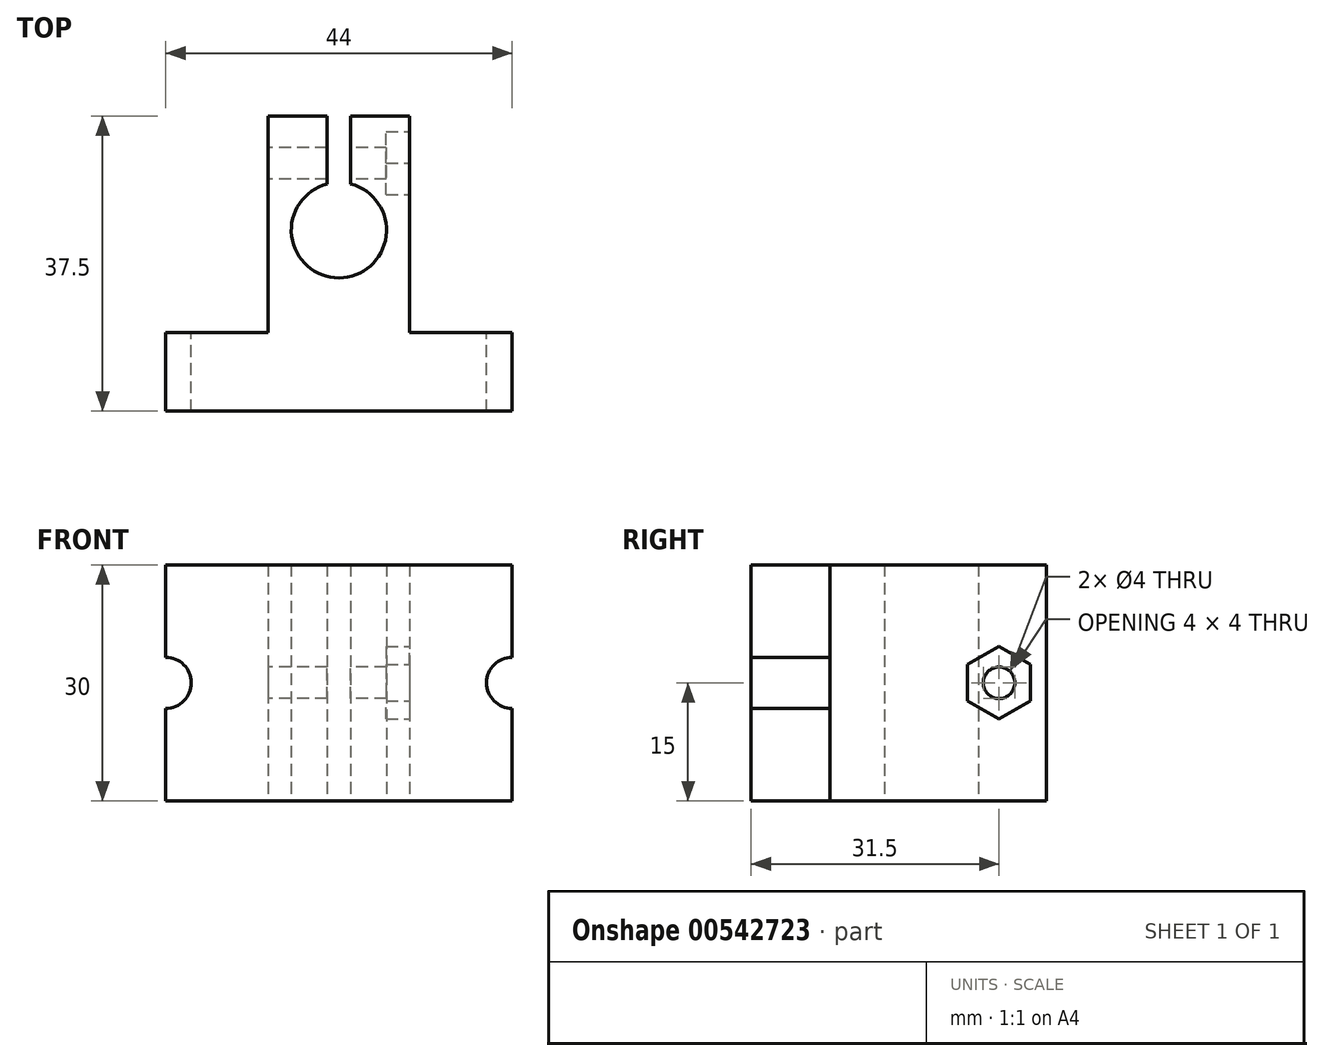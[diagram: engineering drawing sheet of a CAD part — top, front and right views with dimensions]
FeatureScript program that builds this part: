
annotation { "Feature Type Name" : "Feature", "Feature Type Description" : "" }
export const myFeature = defineFeature(function(context is Context, id is Id, definition is map)
    precondition{}
    {
        {
            var Q0;
            Q0=qCreatedBy(makeId("Top.planeOp"),FACE);
            var sketch = newSketch(context, id + "F0", { "sketchPlane" : qUnion([Q0])});
            skLineSegment(sketch, "E0", {"start": v(0, 0) * mm, "end": v(22, 0) * mm});
            skLineSegment(sketch, "E1", {"start": v(22, 0) * mm, "end": v(22, 10) * mm});
            skLineSegment(sketch, "E2", {"start": v(22, 10) * mm, "end": v(9, 10) * mm});
            skLineSegment(sketch, "E3", {"start": v(9, 10) * mm, "end": v(9, 37.5) * mm});
            skArc(sketch, "E4", {"start": v(-1.5, 28.86) * mm, "mid": v(0, 16.95) * mm, "end": v(1.5, 28.86) * mm});
            skLineSegment(sketch, "E5", {"start": v(9, 37.5) * mm, "end": v(1.5, 37.5) * mm});
            skLineSegment(sketch, "E6", {"start": v(1.5, 37.5) * mm, "end": v(1.5, 28.86) * mm});
            skLineSegment(sketch, "E7", {"start": v(0, 37.5) * mm, "end": v(0, 0) * mm, "construction": true});
            skLineSegment(sketch, "E8.MirrorCS", {"start": v(0, 0) * mm, "end": v(-22, 0) * mm});
            skLineSegment(sketch, "E9.MirrorCS", {"start": v(-22, 0) * mm, "end": v(-22, 10) * mm});
            skLineSegment(sketch, "E10.MirrorCS", {"start": v(-22, 10) * mm, "end": v(-9, 10) * mm});
            skLineSegment(sketch, "E11.MirrorCS", {"start": v(-9, 10) * mm, "end": v(-9, 37.5) * mm});
            skLineSegment(sketch, "E12.MirrorCS", {"start": v(-9, 37.5) * mm, "end": v(-1.5, 37.5) * mm});
            skLineSegment(sketch, "E13.MirrorCS", {"start": v(-1.5, 37.5) * mm, "end": v(-1.5, 28.86) * mm});
            skSolve(sketch);
        }
        {
            var Q0;
            Q0=makeQuery(id+"F0.imprint","IMPRINT",FACE,{"disambiguationData":[TD([[makeQuery(id+"F0.imprint","IMPRINT",EDGE,{"derivedFrom":sQuery(id+"F0.wireOp",EDGE,"E0")}),1.0]])]});
            extrude(context, id + "F1", {"entities" : qUnion([Q0]), "depth" : 30 * mm, "offsetDistance" : 25 * mm});
        }
        {
            var Q0;
            Q0=makeQuery(id+"F1.opExtrude","SWEPT_FACE",FACE,{"disambiguationData":[OSD([sQuery(id+"F0.wireOp",EDGE,"E10.MirrorCS")])]});
            var sketch = newSketch(context, id + "F2", { "sketchPlane" : qUnion([Q0])});
            skLineSegment(sketch, "E14", {"start": v(16, 15) * mm, "end": v(22, 15) * mm, "construction": true});
            skLineSegment(sketch, "E15.MirrorCS", {"start": v(-16, 15) * mm, "end": v(-22, 15) * mm, "construction": true});
            skSolve(sketch);
        }
        {
            var Q0;
            Q0=sQuery(id+"F2.wireOp",VERTEX,"E14.end");
            var Q1;
            Q1=sQuery(id+"F2.wireOp",VERTEX,"E15.MirrorCS.end");
            var Q2;
            Q2=makeQuery(id+"F1.opExtrude","SWEPT_BODY",BODY,{"disambiguationData":[OSD([sQuery(id+"F0.wireOp",EDGE,"E0"),sQuery(id+"F0.wireOp",EDGE,"E1"),sQuery(id+"F0.wireOp",EDGE,"E2"),sQuery(id+"F0.wireOp",EDGE,"E3"),sQuery(id+"F0.wireOp",EDGE,"E4"),sQuery(id+"F0.wireOp",EDGE,"E5"),sQuery(id+"F0.wireOp",EDGE,"E6"),sQuery(id+"F0.wireOp",EDGE,"E8.MirrorCS"),sQuery(id+"F0.wireOp",EDGE,"E9.MirrorCS"),sQuery(id+"F0.wireOp",EDGE,"E10.MirrorCS"),sQuery(id+"F0.wireOp",EDGE,"E11.MirrorCS"),sQuery(id+"F0.wireOp",EDGE,"E12.MirrorCS"),sQuery(id+"F0.wireOp",EDGE,"E13.MirrorCS")])]});
            hole(context, id + "F3", {"style" : HoleStyle.SIMPLE, "endStyle" : HoleEndStyle.THROUGH, "holeDiameter" : 6.5 * mm, "majorDiameter" : 5 * mm, "isTappedThrough" : true, "tappedDepth" : 5 * mm, "tapClearance" : 3, "locations" : qUnion([Q0, Q1]), "scope" : qUnion([Q2])});
        }
        {
            var Q0;
            Q0=makeQuery(id+"F1.opExtrude","SWEPT_FACE",FACE,{"disambiguationData":[OSD([sQuery(id+"F0.wireOp",EDGE,"E11.MirrorCS")])]});
            var sketch = newSketch(context, id + "F4", { "sketchPlane" : qUnion([Q0])});
            skLineSegment(sketch, "E16", {"start": v(-37.5, 15) * mm, "end": v(-31.5, 15) * mm});
            skSolve(sketch);
        }
        {
            var Q0;
            Q0=sQuery(id+"F4.wireOp",VERTEX,"E16.end");
            var Q1;
            Q1=makeQuery(id+"F1.opExtrude","SWEPT_BODY",BODY,{"disambiguationData":[OSD([sQuery(id+"F0.wireOp",EDGE,"E0"),sQuery(id+"F0.wireOp",EDGE,"E1"),sQuery(id+"F0.wireOp",EDGE,"E2"),sQuery(id+"F0.wireOp",EDGE,"E3"),sQuery(id+"F0.wireOp",EDGE,"E4"),sQuery(id+"F0.wireOp",EDGE,"E5"),sQuery(id+"F0.wireOp",EDGE,"E6"),sQuery(id+"F0.wireOp",EDGE,"E8.MirrorCS"),sQuery(id+"F0.wireOp",EDGE,"E9.MirrorCS"),sQuery(id+"F0.wireOp",EDGE,"E10.MirrorCS"),sQuery(id+"F0.wireOp",EDGE,"E11.MirrorCS"),sQuery(id+"F0.wireOp",EDGE,"E12.MirrorCS"),sQuery(id+"F0.wireOp",EDGE,"E13.MirrorCS")])]});
            hole(context, id + "F5", {"style" : HoleStyle.SIMPLE, "endStyle" : HoleEndStyle.THROUGH, "holeDiameter" : 4 * mm, "isTappedThrough" : true, "tappedDepth" : 5 * mm, "tapClearance" : 3, "locations" : qUnion([Q0]), "scope" : qUnion([Q1])});
        }
        {
            var Q0;
            Q0=makeQuery(id+"F1.opExtrude","SWEPT_FACE",FACE,{"disambiguationData":[OSD([sQuery(id+"F0.wireOp",EDGE,"E3")])]});
            var sketch = newSketch(context, id + "F6", { "sketchPlane" : qUnion([Q0])});
            skCircle(sketch, "E17.cCircle", {"center": v(31.5, 15) * mm, "radius": 4 * mm, "construction": true});
            skLineSegment(sketch, "E17.0", {"start": v(35.5, 17.3) * mm, "end": v(35.5, 12.7) * mm});
            skLineSegment(sketch, "E17.1", {"start": v(35.5, 12.7) * mm, "end": v(31.5, 10.38) * mm});
            skLineSegment(sketch, "E17.2", {"start": v(31.5, 10.38) * mm, "end": v(27.5, 12.7) * mm});
            skLineSegment(sketch, "E17.3", {"start": v(27.5, 12.7) * mm, "end": v(27.5, 17.3) * mm});
            skLineSegment(sketch, "E17.4", {"start": v(27.5, 17.3) * mm, "end": v(31.5, 19.62) * mm});
            skLineSegment(sketch, "E17.5", {"start": v(31.5, 19.62) * mm, "end": v(35.5, 17.3) * mm});
            skPoint(sketch, "E17.0.midPoint", {"position": v(35.5, 15) * mm});
            skSolve(sketch);
        }
        {
            var Q0;
            Q0=makeQuery(id+"F6.imprint","IMPRINT",FACE,{"disambiguationData":[TD([[makeQuery(id+"F6.imprint","IMPRINT",EDGE,{"derivedFrom":sQuery(id+"F6.wireOp",EDGE,"E17.0")}),-1.0]])]});
            extrude(context, id + "F7", {"entities" : qUnion([Q0]), "operationType" : NewBodyOperationType.REMOVE, "oppositeDirection" : true, "depth" : 3 * mm, "offsetDistance" : 25 * mm});
        }
    });
